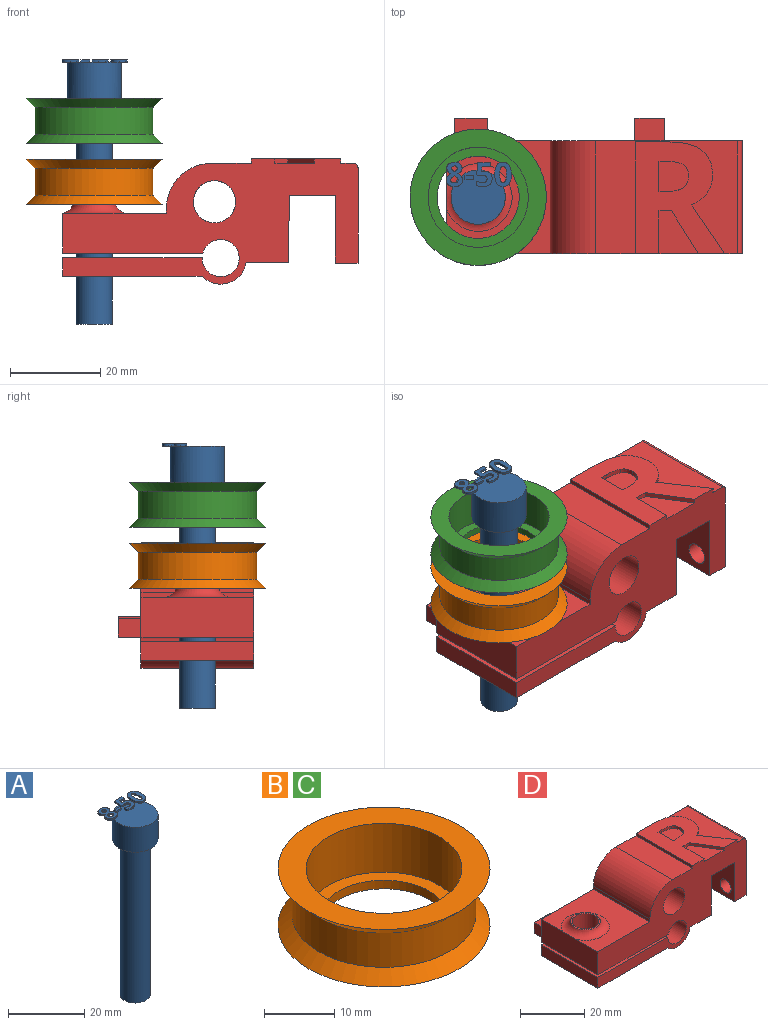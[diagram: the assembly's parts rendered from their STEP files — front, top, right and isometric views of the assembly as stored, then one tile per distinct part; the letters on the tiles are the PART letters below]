
ASSEMBLY  parts=4 mates=2
PART A: 86 faces, bbox 14.5x13.7x58.5 mm
  f0: plane 12x12mm, normal (0,0,1), area 99.4mm2, adj f5,f22,f23,f24,f25,f26,f40,f41
  f1: plane 1x0.26mm, normal (0,0,1), area 0.1mm2, adj f5,f46,f47,f48,f49
  f2: plane 0.85x0.68mm, normal (0,0,1), area 0.2mm2, adj f5,f29,f30,f31
  f3: cylinder r=4mm len=50mm, axis (0,0,-1), area 1256.6mm2, adj f4,f6
  f4: plane 8x8mm, normal (0,0,-1), area 50.3mm2, adj f3
  f5: cylinder r=6mm len=12mm, axis (0,0,-1), area 301.6mm2, adj f0,f1,f2,f6,f39,f45,f67,f85
  f6: plane 12x12mm, normal (0,0,-1), area 62.8mm2, adj f3,f5
  f7: extruded ~0.5x0.46mm, area 0.2mm2, adj f8,f37,f38,f39
  f8: extruded ~0.5x0.46mm, area 0.2mm2, adj f7,f9,f38,f39
  f9: extruded ~0.5x0.39mm, area 0.2mm2, adj f8,f10,f38,f39
  f10: extruded ~0.5x0.4mm, area 0.2mm2, adj f9,f11,f38,f39
  f11: extruded ~0.5x0.49mm, area 0.3mm2, adj f10,f12,f38,f39
  f12: extruded ~0.5x0.5mm, area 0.3mm2, adj f11,f13,f38,f39
  f13: extruded ~0.5x0.39mm, area 0.2mm2, adj f12,f37,f38,f39
  f14: extruded ~1.22x0.5mm, area 0.6mm2, adj f15,f35,f38,f39
  f15: extruded ~1.22x0.5mm, area 0.6mm2, adj f14,f16,f38,f39
  f16: extruded ~0.91x0.5mm, area 0.5mm2, adj f15,f17,f38,f39
  f17: extruded ~0.71x0.5mm, area 0.4mm2, adj f16,f18,f38,f39
  f18: extruded ~0.65x0.61mm, area 0.4mm2, adj f17,f19,f38,f39
  f19: extruded ~0.77x0.62mm, area 0.5mm2, adj f18,f20,f38,f39
  f20: extruded ~0.8x0.5mm, area 0.4mm2, adj f19,f21,f38,f39
  f21: extruded ~1.04x0.5mm, area 0.6mm2, adj f20,f22,f38,f39
  f22: extruded ~1.36x0.5mm, area 0.7mm2, adj f0,f21,f23,f38,f39
  f23: extruded ~1.33x0.5mm, area 0.7mm2, adj f0,f22,f24,f38
  f24: extruded ~1.04x0.51mm, area 0.6mm2, adj f0,f23,f25,f38
  f25: extruded ~0.75x0.5mm, area 0.4mm2, adj f0,f24,f26,f38
  f26: extruded ~0.85x0.66mm, area 0.5mm2, adj f0,f25,f27,f38,f39
  f27: extruded ~0.72x0.56mm, area 0.5mm2, adj f26,f28,f38,f39
  f28: extruded ~0.72x0.5mm, area 0.4mm2, adj f27,f35,f38,f39
  f29: extruded ~0.5x0.45mm, area 0.3mm2, adj f2,f30,f36,f38,f39
  f30: extruded ~0.5x0.47mm, area 0.3mm2, adj f2,f29,f31,f38
  f31: extruded ~0.62x0.5mm, area 0.3mm2, adj f2,f30,f32,f38,f39
  f32: extruded ~0.59x0.5mm, area 0.3mm2, adj f31,f33,f38,f39
  f33: extruded ~0.5x0.48mm, area 0.3mm2, adj f32,f34,f38,f39
  f34: extruded ~0.89x0.77mm, area 0.6mm2, adj f33,f36,f38,f39
  f35: extruded ~0.93x0.5mm, area 0.5mm2, adj f14,f28,f38,f39
  f36: extruded ~0.66x0.5mm, area 0.4mm2, adj f29,f34,f38,f39
  f37: extruded ~0.5x0.39mm, area 0.2mm2, adj f7,f13,f38,f39
  f38: plane 5.4x3.69mm, normal (0,0,1), area 12.7mm2, adj f7,f8,f9,f10,f11,f12,f13,f14
  f39: plane 5.4x3.53mm, normal (0,0,-1), area 10.2mm2, adj f5,f7,f8,f9,f10,f11,f12,f13
  f40: plane 0.9x0.5mm, normal (-1,0,0), area 0.4mm2, adj f0,f41,f43,f44
  f41: plane 1.93x0.5mm, normal (0,-1,0), area 1mm2, adj f0,f40,f42,f44
  f42: plane 0.9x0.5mm, normal (1,0,0), area 0.4mm2, adj f0,f41,f43,f44
  f43: plane 1.93x0.5mm, normal (0,1,0), area 1mm2, adj f0,f40,f42,f44
  f44: plane 1.93x0.9mm, normal (0,0,1), area 1.7mm2, adj f40,f41,f42,f43
  f45: plane 0.76x0.31mm, normal (0,0,-1), area 0mm2, adj f5,f46
  f46: extruded ~1.21x0.5mm, area 0.7mm2, adj f0,f1,f45,f47,f65,f66
  f47: extruded ~0.54x0.5mm, area 0.3mm2, adj f1,f46,f48,f66
  f48: plane 0.5x0.13mm, normal (-0.2,0.98,0), area 0.1mm2, adj f1,f47,f49,f66
  f49: plane 1.03x0.5mm, normal (1,-0.09,0), area 0.5mm2, adj f1,f48,f50,f66,f67
  f50: plane 1.88x0.5mm, normal (0,-1,0), area 0.9mm2, adj f49,f51,f66,f67
  f51: plane 0.94x0.5mm, normal (1,0,0), area 0.5mm2, adj f50,f52,f66,f67
  f52: plane 2.85x0.5mm, normal (0,1,0), area 1.4mm2, adj f51,f53,f66,f67
  f53: plane 2.68x0.5mm, normal (-1,0.07,0), area 1.3mm2, adj f0,f52,f54,f66,f67
  f54: plane 0.5x0.44mm, normal (-0.47,-0.88,0), area 0.3mm2, adj f0,f53,f55,f66
  f55: extruded ~0.5x0.37mm, area 0.2mm2, adj f0,f54,f56,f66
  f56: extruded ~0.5x0.42mm, area 0.2mm2, adj f0,f55,f57,f66
  f57: extruded ~1.05x0.8mm, area 0.8mm2, adj f0,f56,f58,f66
  f58: extruded ~1.02x0.83mm, area 0.8mm2, adj f0,f57,f59,f66
  f59: extruded ~0.72x0.5mm, area 0.4mm2, adj f0,f58,f60,f66
  f60: extruded ~0.66x0.5mm, area 0.4mm2, adj f0,f59,f61,f66
  f61: plane 0.96x0.5mm, normal (-1,0,0), area 0.5mm2, adj f0,f60,f62,f66
  f62: extruded ~1.42x0.5mm, area 0.7mm2, adj f0,f61,f63,f66
  f63: extruded ~1.55x0.5mm, area 0.8mm2, adj f0,f62,f64,f66
  f64: extruded ~1.36x0.54mm, area 0.8mm2, adj f0,f63,f65,f66
  f65: extruded ~1.17x0.5mm, area 0.6mm2, adj f0,f46,f64,f66
  f66: plane 5.33x3.51mm, normal (0,0,1), area 10.9mm2, adj f46,f47,f48,f49,f50,f51,f52,f53
  f67: plane 2.97x1.71mm, normal (0,0,-1), area 3.5mm2, adj f5,f49,f50,f51,f52,f53
  f68: extruded ~1.39x0.5mm, area 0.7mm2, adj f69,f83,f84,f85
  f69: extruded ~1.39x0.5mm, area 0.7mm2, adj f68,f70,f84,f85
  f70: extruded ~0.56x0.5mm, area 0.4mm2, adj f69,f71,f84,f85
  f71: extruded ~0.56x0.5mm, area 0.4mm2, adj f70,f72,f84,f85
  f72: extruded ~1.39x0.5mm, area 0.7mm2, adj f71,f73,f84,f85
  f73: extruded ~1.38x0.5mm, area 0.7mm2, adj f72,f74,f84,f85
  f74: extruded ~0.56x0.5mm, area 0.4mm2, adj f73,f83,f84,f85
  f75: extruded ~2.04x0.5mm, area 1.1mm2, adj f76,f82,f84,f85
  f76: extruded ~2.02x0.5mm, area 1.1mm2, adj f75,f77,f84,f85
  f77: extruded ~1.38x0.69mm, area 0.8mm2, adj f76,f78,f84,f85
  f78: extruded ~1.38x0.66mm, area 0.8mm2, adj f77,f79,f84,f85
  f79: extruded ~2.05x0.5mm, area 1.1mm2, adj f78,f80,f84,f85
  f80: extruded ~2.02x0.5mm, area 1mm2, adj f0,f79,f81,f84,f85
  f81: extruded ~1.37x0.68mm, area 0.8mm2, adj f0,f80,f82,f84
  f82: extruded ~1.39x0.66mm, area 0.8mm2, adj f0,f75,f81,f84,f85
  f83: extruded ~0.56x0.5mm, area 0.4mm2, adj f68,f74,f84,f85
  f84: plane 5.41x3.68mm, normal (0,0,1), area 12.1mm2, adj f68,f69,f70,f71,f72,f73,f74,f75
  f85: plane 5.41x3.68mm, normal (0,0,-1), area 10.3mm2, adj f5,f68,f69,f70,f71,f72,f73,f74
PART B: 8 faces, bbox 30.2x30.2x10 mm
  f0: plane 30.2x30.2mm, normal (0,0,1), area 329.2mm2, adj f1,f7
  f1: cylinder r=11.1mm len=22.2mm, axis (0,0,-1), area 592.8mm2, adj f0,f2
  f2: plane 22.2x22.2mm, normal (0,0,1), area 126.9mm2, adj f1,f3
  f3: cylinder r=9.1mm len=18.2mm, axis (0,0,-1), area 85.8mm2, adj f2,f4
  f4: plane 30.2x30.2mm, normal (0,0,-1), area 456.2mm2, adj f3,f5
  f5: cone r=13.1mm half-angle=45deg, axis (0,0,-1), area 250.6mm2, adj f4,f6
  f6: cylinder r=13.1mm len=26.2mm, axis (0,0,-1), area 493.9mm2, adj f5,f7
  f7: cone r=15.1mm half-angle=45deg, axis (0,0,1), area 250.6mm2, adj f0,f6
PART C: same geometry as B
PART D: 56 faces, bbox 68.9x30x27.7 mm
  f0: plane 31.42x25mm, normal (0,0,1), area 392.1mm2, adj f14,f15,f25,f27,f40,f41,f42,f43
  f1: plane 9.51x8.71mm, normal (0,0,1), area 54.7mm2, adj f14,f37,f38,f39
  f2: plane 25x4.12mm, normal (-1,0,0), area 103mm2, adj f5,f14,f15,f19
  f3: cylinder r=4.17mm len=8.35mm, axis (0,0,1), area 108.1mm2, adj f5,f19
  f4: plane 25x9.34mm, normal (0,0,-1), area 233.4mm2, adj f13,f14,f15,f17
  f5: plane 30.88x25mm, normal (0,0,-1), area 717.2mm2, adj f2,f3,f14,f15,f17
  f6: plane 25x8.82mm, normal (-1,0,0), area 219.6mm2, adj f7,f14,f15,f20,f24
  f7: plane 25x23mm, normal (0,0,1), area 400mm2, adj f6,f8,f14,f15,f24
  f8: plane 25x1.1mm, normal (-1,0,0), area 27.5mm2, adj f7,f14,f15,f25
  f9: plane 25x21.09mm, normal (1,0,0), area 493.5mm2, adj f10,f14,f15,f22,f23,f27
  f10: plane 25x5mm, normal (0,0,-1), area 125mm2, adj f9,f11,f14,f15
  f11: plane 25x15mm, normal (-1,0,0), area 341.3mm2, adj f10,f12,f14,f15,f22,f23
  f12: plane 25x10.2mm, normal (0,0,-1), area 255mm2, adj f11,f13,f14,f15
  f13: plane 25x14.91mm, normal (1,0,-0.01), area 372.8mm2, adj f4,f12,f14,f15
  f14: plane 65.42x27.75mm, normal (0,-1,0), area 997.9mm2, adj f0,f1,f2,f4,f5,f6,f7,f8
  f15: plane 65.42x26.75mm, normal (0,1,0), area 926.8mm2, adj f0,f2,f4,f5,f6,f7,f8,f9
  f16: cylinder r=4.17mm len=10.78mm, axis (0,0,1), area 282.8mm2, adj f20,f21
  f17: cylinder r=5.75mm len=25mm, axis (0,-1,0), area 315.9mm2, adj f4,f5,f14,f15
  f18: cylinder r=4.1mm len=25mm, axis (0,-1,0), area 618.7mm2, adj f14,f15,f19,f20
  f19: plane 30.91x25mm, normal (0,0,1), area 718.1mm2, adj f2,f3,f14,f15,f18
  f20: plane 31.07x30mm, normal (0,0,-1), area 758.4mm2, adj f6,f14,f15,f16,f18,f29,f30,f31
  f21: plane 9.35x9.35mm, normal (0,0,1), area 13.9mm2, adj f16,f24
  f22: cylinder r=2.43mm len=5mm, axis (1,0,0), area 76.2mm2, adj f9,f11
  f23: cylinder r=2.2mm len=5mm, axis (1,0,0), area 69.1mm2, adj f9,f11
  f24: torus R=7.5mm, axis (0,0,-1), area 134.6mm2, adj f6,f7,f21
  f25: cylinder r=10mm len=25mm, axis (0,-1,0), area 392.7mm2, adj f0,f8,f14,f15
  f26: cylinder r=4.68mm len=25mm, axis (0,-1,0), area 735.2mm2, adj f14,f15
  f27: cylinder r=1mm len=25mm, axis (0,-1,0), area 39.3mm2, adj f0,f9,f14,f15
  f28: plane 7.3x5mm, normal (0,0,1), area 36.5mm2, adj f15,f29,f30,f31
  f29: plane 5x4.12mm, normal (-1,0,0), area 20.6mm2, adj f15,f20,f28,f31
  f30: plane 5x4.12mm, normal (1,0,0), area 20.6mm2, adj f15,f20,f28,f31
  f31: plane 7.3x4.12mm, normal (0,1,0), area 30.1mm2, adj f20,f28,f29,f30
  f32: plane 6.63x5mm, normal (0,0,1), area 33.2mm2, adj f15,f33,f35,f36
  f33: plane 5x4.5mm, normal (-1,0,0), area 22.5mm2, adj f15,f32,f34,f36
  f34: plane 6.63x5mm, normal (0,0,-1), area 33.2mm2, adj f15,f33,f35,f36
  f35: plane 5x4.5mm, normal (1,0,0), area 22.5mm2, adj f15,f32,f34,f36
  f36: plane 6.63x4.5mm, normal (0,1,0), area 29.9mm2, adj f32,f33,f34,f35
  f37: plane 9.51x1mm, normal (1,0,0), area 9.5mm2, adj f1,f14,f38,f54
  f38: plane 2.79x1mm, normal (0,-1,0), area 2.8mm2, adj f1,f37,f39,f54
  f39: plane 9.51x5.92mm, normal (-0.85,-0.53,0), area 11.2mm2, adj f1,f14,f38,f54
  f40: extruded ~10.8x7.29mm, area 13mm2, adj f0,f14,f41,f54
  f41: extruded ~3.41x2.67mm, area 4.4mm2, adj f0,f40,f42,f54
  f42: extruded ~3.89x1.2mm, area 4.1mm2, adj f0,f41,f43,f54
  f43: extruded ~5.59x2.42mm, area 6.3mm2, adj f0,f42,f44,f54
  f44: extruded ~7.48x1.84mm, area 7.8mm2, adj f0,f43,f45,f54
  f45: plane 7.22x1mm, normal (0,1,0), area 7.2mm2, adj f0,f44,f46,f54
  f46: plane 24.79x1mm, normal (-1,0,0), area 24.8mm2, adj f0,f14,f45,f54
  f47: plane 1.69x1mm, normal (0,1,0), area 1.7mm2, adj f48,f53,f54,f55
  f48: plane 6.7x1mm, normal (1,0,0), area 6.7mm2, adj f47,f49,f54,f55
  f49: plane 1.6x1mm, normal (0,-1,0), area 1.6mm2, adj f48,f50,f54,f55
  f50: extruded ~3.75x1mm, area 3.9mm2, adj f49,f51,f54,f55
  f51: extruded ~2.51x1.21mm, area 2.9mm2, adj f50,f52,f54,f55
  f52: extruded ~2.61x1.19mm, area 3mm2, adj f51,f53,f54,f55
  f53: extruded ~3.68x1mm, area 3.8mm2, adj f47,f52,f54,f55
  f54: plane 24.79x19.8mm, normal (0,0,1), area 300mm2, adj f14,f37,f38,f39,f40,f41,f42,f43
  f55: plane 6.7x6.56mm, normal (0,0,1), area 38.8mm2, adj f47,f48,f49,f50,f51,f52,f53
PLACE A t=(-103.78,-12.5,-13.6)mm
PLACE B t=(-103.78,-12.5,18.1)mm
PLACE C t=(-103.78,-12.5,31.6)mm
PLACE D at identity
MATE fastened A.f3 <-> C.f1  axis (0,0,-1) through (-103.78,-12.5,36.4)mm
MATE fastened B.f1 <-> D.f3  axis (0,0,-1) through (-103.78,-12.5,12.9)mm
